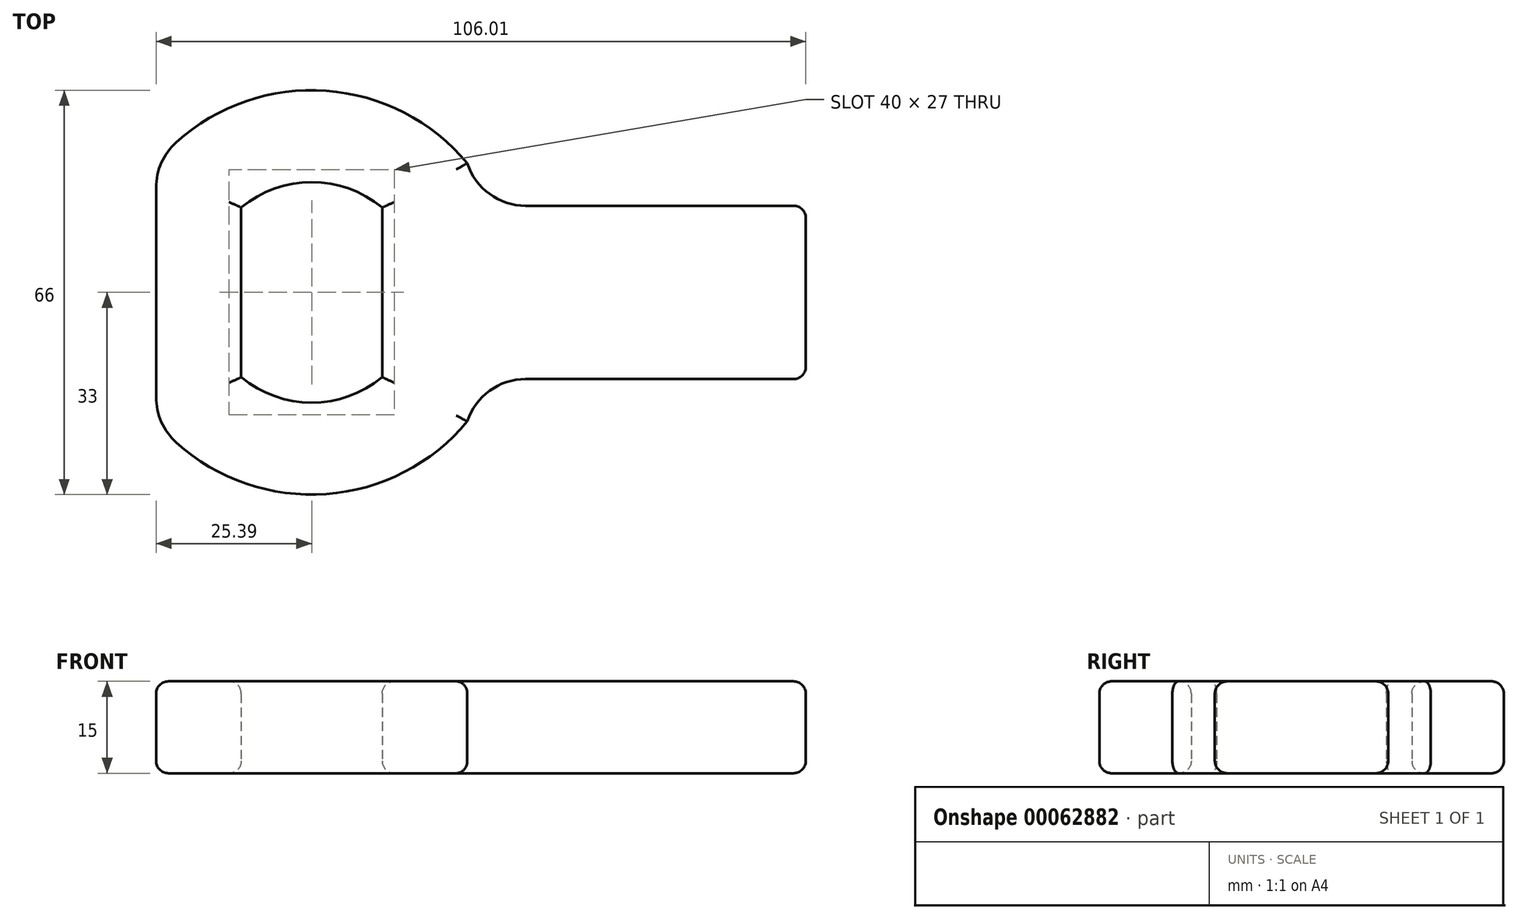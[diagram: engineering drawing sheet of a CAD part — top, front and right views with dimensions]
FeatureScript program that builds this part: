
annotation { "Feature Type Name" : "Feature", "Feature Type Description" : "" }
export const myFeature = defineFeature(function(context is Context, id is Id, definition is map)
    precondition{}
    {
        {
            var Q0;
            Q0=qCreatedBy(makeId("Top.planeOp"),FACE);
            var sketch = newSketch(context, id + "F0", { "sketchPlane" : qUnion([Q0])});
            skArc(sketch, "E0", {"start": v(-11.5, -13.85) * mm, "mid": v(0, -18) * mm, "end": v(11.5, -13.85) * mm});
            skLineSegment(sketch, "E1.rect.left", {"start": v(11.5, 13.85) * mm, "end": v(11.5, -13.85) * mm});
            skLineSegment(sketch, "E1.rect.right", {"start": v(-11.5, 13.85) * mm, "end": v(-11.5, -13.85) * mm});
            skArc(sketch, "E2", {"start": v(-25.4, -21.08) * mm, "mid": v(0, -33) * mm, "end": v(25.4, -21.08) * mm});
            skLineSegment(sketch, "E3.rect.left", {"start": v(-25.4, 21.08) * mm, "end": v(-25.4, -21.08) * mm});
            skLineSegment(sketch, "E3.rect.right", {"start": v(25.4, 21.08) * mm, "end": v(25.4, 14.15) * mm});
            skArc(sketch, "E4.trimOffspring", {"start": v(25.4, 21.08) * mm, "mid": v(0, 33) * mm, "end": v(-25.4, 21.08) * mm});
            skArc(sketch, "E5.trimOffspring", {"start": v(11.5, 13.85) * mm, "mid": v(0, 18) * mm, "end": v(-11.5, 13.85) * mm});
            skLineSegment(sketch, "E6.rect.bottom", {"start": v(80.62, 14.15) * mm, "end": v(25.4, 14.15) * mm});
            skLineSegment(sketch, "E6.rect.top", {"start": v(80.62, -14.15) * mm, "end": v(25.4, -14.15) * mm});
            skLineSegment(sketch, "E6.rect.left", {"start": v(80.62, 14.15) * mm, "end": v(80.62, -14.15) * mm});
            skPoint(sketch, "E6.rect.middle", {"position": v(25.4, 0) * mm});
            skPoint(sketch, "E6.rect.right.start.orphan", {"position": v(-29.84, 14.15) * mm});
            skPoint(sketch, "E7.orphan", {"position": v(-29.84, -14.15) * mm});
            skLineSegment(sketch, "E8.trimOffspring", {"start": v(25.4, -14.15) * mm, "end": v(25.4, -21.08) * mm});
            skSolve(sketch);
        }
        {
            var Q0;
            Q0 = qSketchRegion(id + "F0", true);
            extrude(context, id + "F1", {"entities" : qUnion([Q0]), "depth" : 15 * mm});
        }
        {
            var Q0;
            Q0=makeQuery(id+"F1.opExtrude","SWEPT_EDGE",EDGE,{"disambiguationData":[OSD([sQuery(id+"F0.wireOp",EDGE,"E3.rect.right"),sQuery(id+"F0.wireOp",EDGE,"E6.rect.bottom")])]});
            var Q1;
            Q1=makeQuery(id+"F1.opExtrude","SWEPT_EDGE",EDGE,{"disambiguationData":[OSD([sQuery(id+"F0.wireOp",EDGE,"E6.rect.top"),sQuery(id+"F0.wireOp",EDGE,"E8.trimOffspring")])]});
            var Q2;
            Q2=makeQuery(id+"F1.opExtrude","SWEPT_EDGE",EDGE,{"disambiguationData":[OSD([sQuery(id+"F0.wireOp",EDGE,"E3.rect.left"),sQuery(id+"F0.wireOp",EDGE,"E4.trimOffspring")])]});
            var Q3;
            Q3=makeQuery(id+"F1.opExtrude","SWEPT_EDGE",EDGE,{"disambiguationData":[OSD([sQuery(id+"F0.wireOp",EDGE,"E2"),sQuery(id+"F0.wireOp",EDGE,"E3.rect.left")])]});
            fillet(context, id + "F2", {"entities" : qUnion([Q0, Q1, Q2, Q3]), "radius" : 10 * mm, "tangentPropagation" : true, "allowEdgeOverflow" : false});
        }
        {
            var Q0;
            Q0=makeQuery(id+"F1.opExtrude","SWEPT_EDGE",EDGE,{"disambiguationData":[OSD([sQuery(id+"F0.wireOp",EDGE,"E6.rect.top"),sQuery(id+"F0.wireOp",EDGE,"E6.rect.left")])]});
            var Q1;
            Q1=makeQuery(id+"F1.opExtrude","SWEPT_EDGE",EDGE,{"disambiguationData":[OSD([sQuery(id+"F0.wireOp",EDGE,"E6.rect.bottom"),sQuery(id+"F0.wireOp",EDGE,"E6.rect.left")])]});
            var Q2;
            Q2=makeQuery(id+"F1.opExtrude","CAP_EDGE",EDGE,{"disambiguationData":[OSD([sQuery(id+"F0.wireOp",EDGE,"E1.rect.left")])],"isStart":false});
            var Q3;
            Q3=makeQuery(id+"F1.opExtrude","CAP_EDGE",EDGE,{"disambiguationData":[OSD([sQuery(id+"F0.wireOp",EDGE,"E1.rect.right")])],"isStart":false});
            var Q4;
            Q4=makeQuery(id+"F1.opExtrude","CAP_EDGE",EDGE,{"disambiguationData":[OSD([sQuery(id+"F0.wireOp",EDGE,"E5.trimOffspring")])],"isStart":false});
            var Q5;
            Q5=makeQuery(id+"F1.opExtrude","CAP_EDGE",EDGE,{"disambiguationData":[OSD([sQuery(id+"F0.wireOp",EDGE,"E0")])],"isStart":false});
            var Q6;
            Q6=makeQuery(id+"F1.opExtrude","CAP_FACE",FACE,{"disambiguationData":[OSD([sQuery(id+"F0.wireOp",EDGE,"E0"),sQuery(id+"F0.wireOp",EDGE,"E1.rect.left"),sQuery(id+"F0.wireOp",EDGE,"E1.rect.right"),sQuery(id+"F0.wireOp",EDGE,"E2"),sQuery(id+"F0.wireOp",EDGE,"E3.rect.left"),sQuery(id+"F0.wireOp",EDGE,"E3.rect.right"),sQuery(id+"F0.wireOp",EDGE,"E4.trimOffspring"),sQuery(id+"F0.wireOp",EDGE,"E5.trimOffspring"),sQuery(id+"F0.wireOp",EDGE,"E6.rect.bottom"),sQuery(id+"F0.wireOp",EDGE,"E6.rect.top"),sQuery(id+"F0.wireOp",EDGE,"E6.rect.left"),sQuery(id+"F0.wireOp",EDGE,"E8.trimOffspring")])],"isStart":false});
            var Q7;
            Q7=makeQuery(id+"F1.opExtrude","CAP_FACE",FACE,{"disambiguationData":[OSD([sQuery(id+"F0.wireOp",EDGE,"E0"),sQuery(id+"F0.wireOp",EDGE,"E1.rect.left"),sQuery(id+"F0.wireOp",EDGE,"E1.rect.right"),sQuery(id+"F0.wireOp",EDGE,"E2"),sQuery(id+"F0.wireOp",EDGE,"E3.rect.left"),sQuery(id+"F0.wireOp",EDGE,"E3.rect.right"),sQuery(id+"F0.wireOp",EDGE,"E4.trimOffspring"),sQuery(id+"F0.wireOp",EDGE,"E5.trimOffspring"),sQuery(id+"F0.wireOp",EDGE,"E6.rect.bottom"),sQuery(id+"F0.wireOp",EDGE,"E6.rect.top"),sQuery(id+"F0.wireOp",EDGE,"E6.rect.left"),sQuery(id+"F0.wireOp",EDGE,"E8.trimOffspring")])],"isStart":true});
            fillet(context, id + "F3", {"entities" : qUnion([Q0, Q1, Q2, Q3, Q4, Q5, Q6, Q7]), "radius" : 2 * mm, "tangentPropagation" : true, "allowEdgeOverflow" : false});
        }
    });
